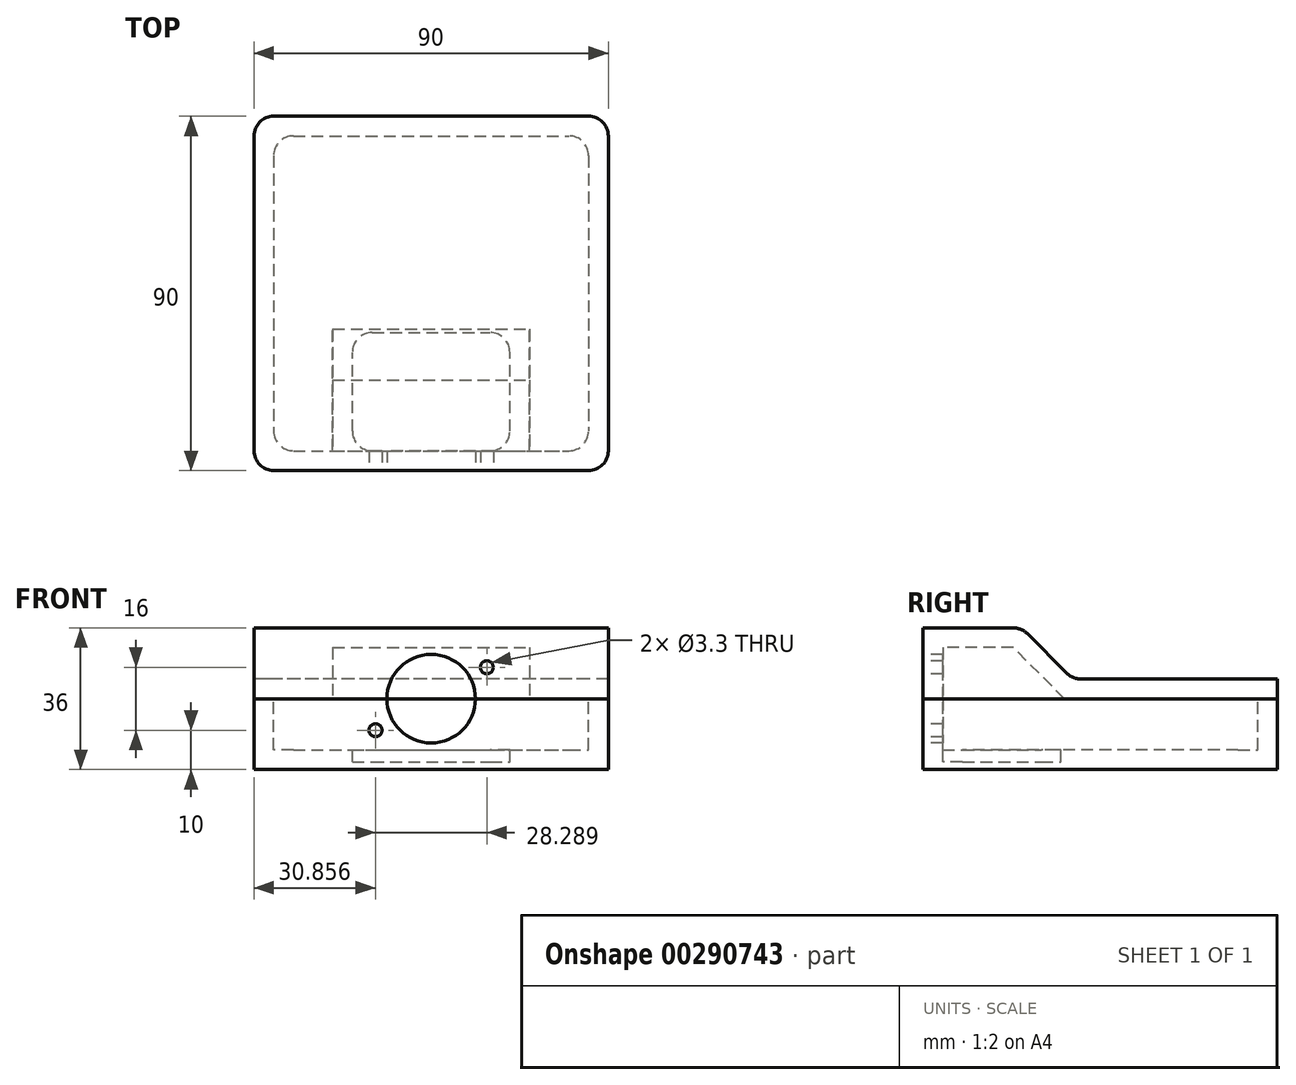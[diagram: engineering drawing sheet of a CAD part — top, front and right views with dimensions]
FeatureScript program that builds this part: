
annotation { "Feature Type Name" : "Feature", "Feature Type Description" : "" }
export const myFeature = defineFeature(function(context is Context, id is Id, definition is map)
    precondition{}
    {
        {
            var Q0;
            Q0=qCreatedBy(makeId("Right.planeOp"),FACE);
            var sketch = newSketch(context, id + "F0", { "sketchPlane" : qUnion([Q0])});
            skLineSegment(sketch, "E0.bottom", {"start": v(-45, 0) * mm, "end": v(45, 0) * mm});
            skLineSegment(sketch, "E0.top", {"start": v(-45, -18) * mm, "end": v(45, -18) * mm});
            skLineSegment(sketch, "E0.left", {"start": v(-45, 0) * mm, "end": v(-45, -18) * mm});
            skLineSegment(sketch, "E0.right", {"start": v(45, 0) * mm, "end": v(45, -18) * mm});
            skPoint(sketch, "E0.middle", {"position": v(0, -9) * mm});
            skSolve(sketch);
        }
        {
            var Q0;
            Q0 = qSketchRegion(id + "F0", true);
            extrude(context, id + "F1", {"entities" : qUnion([Q0]), "endBound" : BoundingType.SYMMETRIC, "depth" : 90 * mm});
        }
        {
            var Q0;
            Q0=qCreatedBy(makeId("Right.planeOp"),FACE);
            var sketch = newSketch(context, id + "F2", { "sketchPlane" : qUnion([Q0])});
            skLineSegment(sketch, "E1.bottom", {"start": v(-45, 0) * mm, "end": v(45, 0) * mm});
            skLineSegment(sketch, "E1.left", {"start": v(-45, 0) * mm, "end": v(-45, 18) * mm});
            skLineSegment(sketch, "E1.right", {"start": v(45, 0) * mm, "end": v(45, 5) * mm});
            skLineSegment(sketch, "E2", {"start": v(-45, 18) * mm, "end": v(-20, 18) * mm});
            skLineSegment(sketch, "E3", {"start": v(-20, 18) * mm, "end": v(-7, 5) * mm});
            skLineSegment(sketch, "E4", {"start": v(-7, 5) * mm, "end": v(45, 5) * mm});
            skSolve(sketch);
        }
        {
            var Q0;
            Q0=makeQuery(id+"F2.imprint","IMPRINT",FACE,{"disambiguationData":[TD([[makeQuery(id+"F2.imprint","IMPRINT",EDGE,{"derivedFrom":sQuery(id+"F2.wireOp",EDGE,"E1.bottom")}),1.0]])]});
            extrude(context, id + "F3", {"entities" : qUnion([Q0]), "endBound" : BoundingType.SYMMETRIC, "depth" : 90 * mm});
        }
        {
            var Q0;
            Q0=makeQuery(id+"F1.opExtrude","SWEPT_FACE",FACE,{"disambiguationData":[OSD([sQuery(id+"F0.wireOp",EDGE,"E0.bottom")])]});
            var sketch = newSketch(context, id + "F4", { "sketchPlane" : qUnion([Q0])});
            skLineSegment(sketch, "E5.bottom", {"start": v(-40, 40) * mm, "end": v(40, 40) * mm});
            skLineSegment(sketch, "E5.top", {"start": v(-40, -40) * mm, "end": v(40, -40) * mm});
            skLineSegment(sketch, "E5.left", {"start": v(-40, 40) * mm, "end": v(-40, -40) * mm});
            skLineSegment(sketch, "E5.right", {"start": v(40, 40) * mm, "end": v(40, -40) * mm});
            skPoint(sketch, "E5.middle", {"position": v(0, 0) * mm});
            skSolve(sketch);
        }
        {
            var Q0;
            Q0=makeQuery(id+"F4.imprint","IMPRINT",FACE,{"disambiguationData":[TD([[makeQuery(id+"F4.imprint","IMPRINT",EDGE,{"derivedFrom":sQuery(id+"F4.wireOp",EDGE,"E5.bottom")}),-1.0]])]});
            extrude(context, id + "F5", {"entities" : qUnion([Q0]), "operationType" : NewBodyOperationType.REMOVE, "oppositeDirection" : true, "depth" : 13 * mm});
        }
        {
            var Q0;
            Q0=makeQuery(id+"F5.boolean.opBoolean","COPY",FACE,{"derivedFrom":makeQuery(id+"F5.opExtrude","CAP_FACE",FACE,{"disambiguationData":[OSD([sQuery(id+"F4.wireOp",EDGE,"E5.bottom"),sQuery(id+"F4.wireOp",EDGE,"E5.top"),sQuery(id+"F4.wireOp",EDGE,"E5.left"),sQuery(id+"F4.wireOp",EDGE,"E5.right")])],"isStart":false})});
            var sketch = newSketch(context, id + "F6", { "sketchPlane" : qUnion([Q0])});
            skLineSegment(sketch, "E6.bottom", {"start": v(-20, -40) * mm, "end": v(20, -40) * mm});
            skLineSegment(sketch, "E6.top", {"start": v(-20, -10) * mm, "end": v(20, -10) * mm});
            skLineSegment(sketch, "E6.left", {"start": v(-20, -40) * mm, "end": v(-20, -10) * mm});
            skLineSegment(sketch, "E6.right", {"start": v(20, -40) * mm, "end": v(20, -10) * mm});
            skPoint(sketch, "E7", {"position": v(0, -40) * mm});
            skSolve(sketch);
        }
        {
            var Q0;
            Q0 = qSketchRegion(id + "F6", true);
            extrude(context, id + "F7", {"entities" : qUnion([Q0]), "operationType" : NewBodyOperationType.REMOVE, "oppositeDirection" : true, "depth" : 3 * mm});
        }
        {
            var Q0;
            Q0=makeQuery(id+"F1.opExtrude","SWEPT_FACE",FACE,{"disambiguationData":[OSD([sQuery(id+"F0.wireOp",EDGE,"E0.left")])]});
            var sketch = newSketch(context, id + "F8", { "sketchPlane" : qUnion([Q0])});
            skPoint(sketch, "E8", {"position": v(0, 0) * mm});
            skPoint(sketch, "E9", {"position": v(-14.14, -8) * mm});
            skPoint(sketch, "E10", {"position": v(14.14, 8) * mm});
            skSolve(sketch);
        }
        {
            var Q0;
            Q0=sQuery(id+"F8.wireOp",VERTEX,"E8");
            var Q1;
            Q1=makeQuery(id+"F1.opExtrude","SWEPT_BODY",BODY,{"disambiguationData":[OSD([sQuery(id+"F0.wireOp",EDGE,"E0.bottom"),sQuery(id+"F0.wireOp",EDGE,"E0.top"),sQuery(id+"F0.wireOp",EDGE,"E0.left"),sQuery(id+"F0.wireOp",EDGE,"E0.right")])]});
            var Q2;
            Q2=makeQuery(id+"F3.opExtrude","SWEPT_BODY",BODY,{"disambiguationData":[OSD([sQuery(id+"F2.wireOp",EDGE,"E1.bottom"),sQuery(id+"F2.wireOp",EDGE,"E1.left"),sQuery(id+"F2.wireOp",EDGE,"E1.right"),sQuery(id+"F2.wireOp",EDGE,"E2"),sQuery(id+"F2.wireOp",EDGE,"E3"),sQuery(id+"F2.wireOp",EDGE,"E4")])]});
            hole(context, id + "F9", {"style" : HoleStyle.SIMPLE, "endStyle" : HoleEndStyle.BLIND, "holeDiameter" : 22.5 * mm, "holeDepth" : 5 * mm, "tappedDepth" : 12 * mm, "tapClearance" : 3, "locations" : qUnion([Q0]), "scope" : qUnion([Q1, Q2])});
        }
        {
            var Q0;
            Q0=qCreatedBy(makeId("Right.planeOp"),FACE);
            var sketch = newSketch(context, id + "F10", { "sketchPlane" : qUnion([Q0])});
            skLineSegment(sketch, "E11", {"start": v(-40, 0) * mm, "end": v(-9.07, 0) * mm});
            skLineSegment(sketch, "E12", {"start": v(-9.07, 0) * mm, "end": v(-22.07, 13) * mm});
            skLineSegment(sketch, "E13", {"start": v(-22.07, 13) * mm, "end": v(-40, 13) * mm});
            skLineSegment(sketch, "E14", {"start": v(-40, 13) * mm, "end": v(-40, 0) * mm});
            skSolve(sketch);
        }
        {
            var Q0;
            Q0 = qSketchRegion(id + "F10", true);
            extrude(context, id + "F11", {"entities" : qUnion([Q0]), "operationType" : NewBodyOperationType.REMOVE, "endBound" : BoundingType.SYMMETRIC, "oppositeDirection" : true, "depth" : 50 * mm});
        }
        {
            var Q0;
            Q0=makeQuery(id+"F3.opExtrude","SWEPT_EDGE",EDGE,{"disambiguationData":[OSD([sQuery(id+"F2.wireOp",EDGE,"E2"),sQuery(id+"F2.wireOp",EDGE,"E3")])]});
            var Q1;
            Q1=makeQuery(id+"F3.opExtrude","SWEPT_EDGE",EDGE,{"disambiguationData":[OSD([sQuery(id+"F2.wireOp",EDGE,"E3"),sQuery(id+"F2.wireOp",EDGE,"E4")])]});
            fillet(context, id + "F12", {"entities" : qUnion([Q0, Q1]), "radius" : 5 * mm, "tangentPropagation" : true, "allowEdgeOverflow" : false});
        }
        {
            var Q0;
            Q0=makeQuery(id+"F3.opExtrude","CAP_EDGE",EDGE,{"disambiguationData":[OSD([sQuery(id+"F2.wireOp",EDGE,"E1.left")])],"isStart":false});
            var Q1;
            Q1=makeQuery(id+"F1.opExtrude","CAP_EDGE",EDGE,{"disambiguationData":[OSD([sQuery(id+"F0.wireOp",EDGE,"E0.left")])],"isStart":false});
            var Q2;
            Q2=makeQuery(id+"F1.opExtrude","CAP_EDGE",EDGE,{"disambiguationData":[OSD([sQuery(id+"F0.wireOp",EDGE,"E0.right")])],"isStart":false});
            var Q3;
            Q3=makeQuery(id+"F3.opExtrude","CAP_EDGE",EDGE,{"disambiguationData":[OSD([sQuery(id+"F2.wireOp",EDGE,"E1.right")])],"isStart":false});
            var Q4;
            Q4=makeQuery(id+"F1.opExtrude","CAP_EDGE",EDGE,{"disambiguationData":[OSD([sQuery(id+"F0.wireOp",EDGE,"E0.right")])],"isStart":true});
            var Q5;
            Q5=makeQuery(id+"F3.opExtrude","CAP_EDGE",EDGE,{"disambiguationData":[OSD([sQuery(id+"F2.wireOp",EDGE,"E1.right")])],"isStart":true});
            var Q6;
            Q6=makeQuery(id+"F3.opExtrude","CAP_EDGE",EDGE,{"disambiguationData":[OSD([sQuery(id+"F2.wireOp",EDGE,"E1.left")])],"isStart":true});
            var Q7;
            Q7=makeQuery(id+"F1.opExtrude","CAP_EDGE",EDGE,{"disambiguationData":[OSD([sQuery(id+"F0.wireOp",EDGE,"E0.left")])],"isStart":true});
            fillet(context, id + "F13", {"entities" : qUnion([Q0, Q1, Q2, Q3, Q4, Q5, Q6, Q7]), "radius" : 5 * mm, "tangentPropagation" : true, "allowEdgeOverflow" : false});
        }
        {
            var Q0;
            Q0=sQuery(id+"F8.wireOp",VERTEX,"E9");
            var Q1;
            Q1=sQuery(id+"F8.wireOp",VERTEX,"E10");
            var Q2;
            Q2=makeQuery(id+"F1.opExtrude","SWEPT_BODY",BODY,{"disambiguationData":[OSD([sQuery(id+"F0.wireOp",EDGE,"E0.bottom"),sQuery(id+"F0.wireOp",EDGE,"E0.top"),sQuery(id+"F0.wireOp",EDGE,"E0.left"),sQuery(id+"F0.wireOp",EDGE,"E0.right")])]});
            var Q3;
            Q3=makeQuery(id+"F3.opExtrude","SWEPT_BODY",BODY,{"disambiguationData":[OSD([sQuery(id+"F2.wireOp",EDGE,"E1.bottom"),sQuery(id+"F2.wireOp",EDGE,"E1.left"),sQuery(id+"F2.wireOp",EDGE,"E1.right"),sQuery(id+"F2.wireOp",EDGE,"E2"),sQuery(id+"F2.wireOp",EDGE,"E3"),sQuery(id+"F2.wireOp",EDGE,"E4")])]});
            hole(context, id + "F14", {"style" : HoleStyle.SIMPLE, "endStyle" : HoleEndStyle.BLIND, "standardTappedOrClearance" : lookupTablePath({ "standard" : "ISO", "fit" : "Normal", "size" : "M3", "type" : "Clearance" }), "standardBlindInLast" : lookupTablePath({ "fit" : "Standard", "standard" : "ISO", "size" : "M3", "type" : "Clearance" }), "holeDiameter" : 3.3 * mm, "holeDepth" : 5 * mm, "tappedDepth" : 12 * mm, "tapClearance" : 3, "locations" : qUnion([Q0, Q1]), "scope" : qUnion([Q2, Q3])});
        }
        {
            var Q0;
            Q0=makeQuery(id+"F5.boolean.opBoolean","COPY",EDGE,{"derivedFrom":makeQuery(id+"F5.opExtrude","SWEPT_EDGE",EDGE,{"disambiguationData":[OSD([sQuery(id+"F4.wireOp",EDGE,"E5.bottom"),sQuery(id+"F4.wireOp",EDGE,"E5.left")])]})});
            var Q1;
            Q1=makeQuery(id+"F5.boolean.opBoolean","COPY",EDGE,{"derivedFrom":makeQuery(id+"F5.opExtrude","SWEPT_EDGE",EDGE,{"disambiguationData":[OSD([sQuery(id+"F4.wireOp",EDGE,"E5.bottom"),sQuery(id+"F4.wireOp",EDGE,"E5.right")])]})});
            var Q2;
            Q2=makeQuery(id+"F5.boolean.opBoolean","COPY",EDGE,{"derivedFrom":makeQuery(id+"F5.opExtrude","SWEPT_EDGE",EDGE,{"disambiguationData":[OSD([sQuery(id+"F4.wireOp",EDGE,"E5.top"),sQuery(id+"F4.wireOp",EDGE,"E5.left")])]})});
            var Q3;
            Q3=makeQuery(id+"F5.boolean.opBoolean","COPY",EDGE,{"derivedFrom":makeQuery(id+"F5.opExtrude","SWEPT_EDGE",EDGE,{"disambiguationData":[OSD([sQuery(id+"F4.wireOp",EDGE,"E5.top"),sQuery(id+"F4.wireOp",EDGE,"E5.right")])]})});
            var Q4;
            Q4=makeQuery(id+"F7.boolean.opBoolean","COPY",EDGE,{"derivedFrom":makeQuery(id+"F7.opExtrude","SWEPT_EDGE",EDGE,{"disambiguationData":[OSD([sQuery(id+"F6.wireOp",EDGE,"E6.top"),sQuery(id+"F6.wireOp",EDGE,"E6.left")])]})});
            var Q5;
            Q5=makeQuery(id+"F7.boolean.opBoolean","COPY",EDGE,{"derivedFrom":makeQuery(id+"F7.opExtrude","SWEPT_EDGE",EDGE,{"disambiguationData":[OSD([sQuery(id+"F6.wireOp",EDGE,"E6.top"),sQuery(id+"F6.wireOp",EDGE,"E6.right")])]})});
            var Q6;
            Q6=makeQuery(id+"F7.boolean.opBoolean","COPY",EDGE,{"derivedFrom":makeQuery(id+"F7.opExtrude","SWEPT_EDGE",EDGE,{"disambiguationData":[OSD([sQuery(id+"F4.wireOp",EDGE,"E5.top"),sQuery(id+"F6.wireOp",EDGE,"E6.bottom"),sQuery(id+"F6.wireOp",EDGE,"E6.right")])]})});
            var Q7;
            Q7=makeQuery(id+"F7.boolean.opBoolean","COPY",EDGE,{"derivedFrom":makeQuery(id+"F7.opExtrude","SWEPT_EDGE",EDGE,{"disambiguationData":[OSD([sQuery(id+"F4.wireOp",EDGE,"E5.top"),sQuery(id+"F6.wireOp",EDGE,"E6.bottom"),sQuery(id+"F6.wireOp",EDGE,"E6.left")])]})});
            fillet(context, id + "F15", {"entities" : qUnion([Q0, Q1, Q2, Q3, Q4, Q5, Q6, Q7]), "radius" : 5 * mm, "tangentPropagation" : true, "allowEdgeOverflow" : false});
        }
    });
